# Revit family: ALTERED 143342_Double-DoubleHung-Grid-5PieceTrim6508
name_source: partatom
category: Windows
revit_build: Autodesk Revit 2016 (Build: 20150220_1215(x64)
units: mm (PartAtom-declared; Revit-internal decimal feet)

## family parameters
Always vertical = Yes
Cut with Voids When Loaded = No
Host = Wall
Room Calculation Point = No
Shared = No

## types (2) — shared parameters
Analytic Construction = <None>
Default Sill Height = 559 mm
Frame Material = Door - Frame
Frame Thickness = 25 mm
Grid Thickness = 13 mm  [stored 0.0426509 ft]
Height = 1829 mm
Lintel Trim 1 Overhang = 25 mm
Lintel Trim 1 Projection = 38 mm
Lintel Trim 1 Width = 89 mm
Lintel Trim 2 Overhang = 25 mm
Lintel Trim 2 Projection = 64 mm
Lintel Trim 2 Width = 25 mm
Rough Height = 1842 mm
Rough Width = 1842 mm
Sash Material = Door - Frame
Sash Thickness = 44 mm
Sill Trim Overhang = 25 mm
Sill Trim Projection = 51 mm
Sill Trim Width = 51 mm
Trim Material = Door - Panel
Trim Projection = 25 mm
Trim Width = 89 mm
Wall Closure = By host
Width = 1829 mm

## per-type parameters (varying)
| type | Window Height |
| 72"x60" | 1524 mm  [stored 5 ft] |
| 72"x72" | 1829 mm |

note: [stored X ft] marks values corroborated as IEEE doubles in the binary element streams (Revit-internal decimal feet)

## geometry (parser evidence)
native form markers: Blend x6, Sweep x11
no freeform markers — native parametric forms only
